# Revit family: ONZ_5BF
name_source: partatom
category: Mechanical Equipment
units: mm (PartAtom-declared; Revit-internal decimal feet)

## family parameters
Always vertical = Yes
Cut with Voids When Loaded = No
OmniClass Number = 23.40.40.11.17
OmniClass Title = Refrigerated Cases
Part Type = Normal
Room Calculation Point = No
Round Connector Dimension = Use Radius
Shared = No
Work Plane-Based = Yes

## types (4) — shared parameters
BASE HEIGHT = 5"
BTU PER FOOT CONVENTIONAL = 426
BTU PER FOOT PARALLEL = 408
CERTIFICATIONS = NSF 7, UL471, CSA
COIL REFRIGERATION CHARGE = 0.00 lb
CONTROL TYPE = T-STAT
DATE = 05/18/12
DEDICATED CIRCUIT = YES
DEFROST PHASE = 1
DEFROST WATTAGE = 0 W
DIEBOARD HEIGHT = 0"
DISCHARGE AIR TEMPERATURE = -2 °F
DRAIN LINE CONNECTION = Drain Connection
DRAIN LINE DIAMETER = 2"
DRAIN LINE RADIUS = 1"
DRAIN PIPE LENGTH = 0"
DRAIN PIPE TYPE = PVC
DRIP PAN PLUMB TYPE = HARD
Default Elevation = 48"
Description = Narrow Single-Deck Island Merchandiser
ELECTRIC DEFROST = No
ELECTRICAL DEFROST VOLTAGE = 0 V
EVAPORATOR TEMPERATURE = -12 °F
FAN CONNECTOR DESCRIPTION = FAN AND ANTI SWEAT CONNECTOR
FAN NUMBER OF POLES = 1
FAN TYPE = ECM
FROZEN CASE = Yes
GROUND FAULT PROTECTION = NO
HEIGHT = 35"
HOT GAS DEFROST = No
ICE CREAM CASE = No
ISOLATED GROUND REQUIRED = NO
Keynote = Frozen Food/ Ice Cream
LED LIGHTING AMPS = 0 A
LED LIGHTING AMPS PER ROW = 0 A
LED LIGHTING WATTAGE = 0 W
LIGHT AMPS = 0 A
LIGHT TYPE = T8 FLUORESCENT
LIGHTING APPARENT LOAD = 0 VA
LIGHTING CONNECTION DESCRIPTION = LIGHTING CONNECTOR
LIGHTING NUMBER OF POLES = 1
LIGHTING WATTAGE = 0 VA
LIQUID LINE CONNECTION = LIQUID LINE CONNECTION
LIQUID LINE DIAMETER = 0"
LIQUID LINE RADIUS = 0"
Manufacturer = HILL PHOENIX
NUMBER OF WIRES = 3
PHASE = 1
POWER FACTOR = 1
PRESSURE REGULATOR = 0.00 psi
REAR LOAD = 24"
RECEPTICAL MOUNTING HEIGHT ABOVE FLOOR = 19 3/4"
REF PIPE LENGTH = 28 5/8"
REF PLANE FRONT BACK = 21 7/16"
REVERSE AIR DEFROST = No
SET BACK MODE FOR ENERGY CONSERVATION = NO
SHELVE LENGTH = 48"
SIZE OF COLD WATER HOOK UP = 0"
SIZE OF HOT WATER HOOK-UP = 0"
SUCTION LINE CONNECTION = SUCTION LINE CONNECTION
SUCTION LINE DIAMETER = 1"
SUCTION LINE RADIUS = 0"
T8 LIGHT OR LED LIGHT = Yes
T8 LIGHTING AMPS = 0 A
T8 LIGHTING AMPS PER ROW = 0 A
T8 LIGHTING WATTAGE = 0 W
TIME OFF DEFROST = Yes
TOEKICK HEIGHT = 5 1/2"
TOEKICK INSET = 1 1/2"
URL = http://www.hillphoenix.com
VOLTAGE = 120 V
WATER LINE MOUNTING HEIGHT ABOVE FLOOR = 0"
WEIGHT = 0.00 lb
WIDTH = 42 7/8"
zero-valued in all types: BTU ADD FOR LIGHTS, BTU ADD PER SHELF PER FOOT, CORNICE AND NOSE LIGHT ROWS, LED LIGHTING BTU ADD PER ROW, SHELF LIGHT ROWS, T8 LIGHTING BTU ADD PER ROW

## per-type parameters (varying)
| type | ANTI SWEAT APPARENT LOAD | ANTI SWEAT HEATER AMPS | ANTI SWEAT HEATER WATTAGE | C CASE DEFROST AMPS | CONVENTIONAL EVAPORATOR LOAD | DEFROST AMPS | F CASE DEFROST AMPS | FAN AMPS | FAN AND ANTI SWEAT HEATER APPARENT LOAD | FAN APPARENT LOAD | FAN QUANTITY | FAN WATTAGE | LEGEND NUMBER | LENGTH | LENGTH FOR BTU | Model | PARALLEL EVAPORATOR LOAD | REF PLANE LEFT RIGHT | TOTAL APPARENT FAN-LIGHT AND A/S LOAD | TOTAL CASE AMPS | TOTAL CASE WATTAGE |
| ONZ-8' | 157 VA | 1 A | 157 W | 12 A | 3408 | 8 A | 8 A | 0 A | 211 VA | 54 VA | 3 | 33 W | ONZ-8' | 100 13/16" | 8 | ONZ-8' | 3264 | 50 7/16" | 190 VA | 2 A | 190 W |
| ONZ-12' | 238 VA | 2 A | 238 W | 17 A | 5112 | 12 A | 12 A | 1 A | 310 VA | 72 VA | 4 | 44 W | ONZ-12' | 144" | 12 | ONZ-12' | 4896 | 72" | 282 VA | 3 A | 282 W |
| ONZ-6' | 238 VA | 2 A | 238 W | 17 A | 2556 | 12 A | 12 A | 1 A | 310 VA | 72 VA | 4 | 44 W | ONZ-12' | 72" | 6 | ONZ-12' | 2448 | 36" | 282 VA | 3 A | 282 W |
| ONZ-10' | 238 VA | 2 A | 238 W | 17 A | 4260 | 12 A | 12 A | 1 A | 310 VA | 72 VA | 4 | 44 W | ONZ-12' | 120" | 10 | ONZ-12' | 4080 | 60" | 282 VA | 3 A | 282 W |

## geometry (parser evidence)
native form markers: Blend x4, Sweep x8
no freeform markers — native parametric forms only
